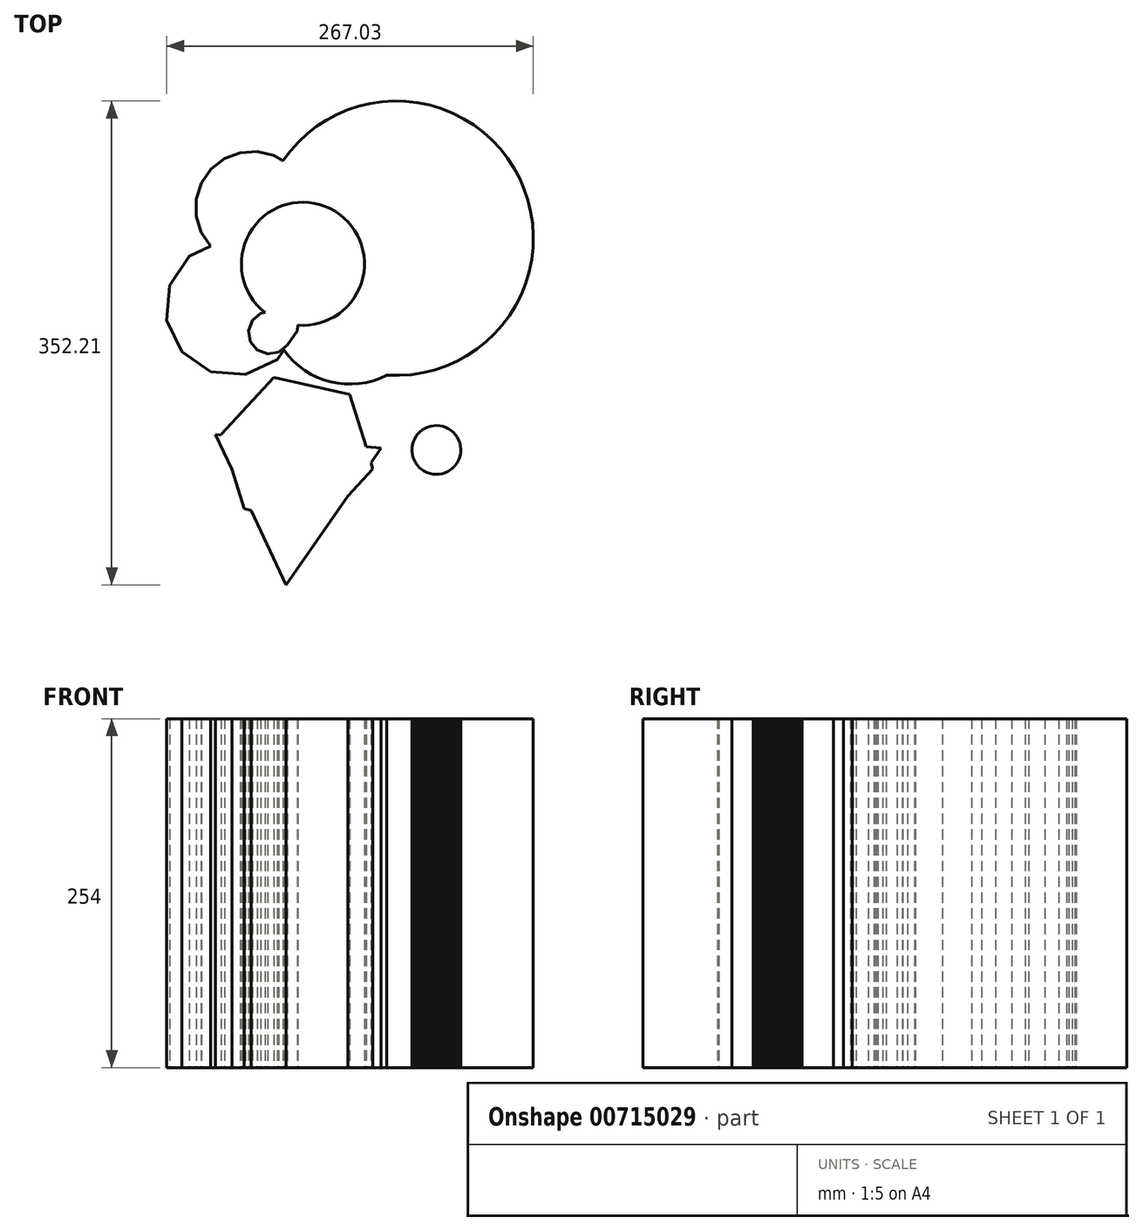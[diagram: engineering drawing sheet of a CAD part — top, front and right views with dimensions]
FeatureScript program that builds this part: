
annotation { "Feature Type Name" : "Feature", "Feature Type Description" : "" }
export const myFeature = defineFeature(function(context is Context, id is Id, definition is map)
    precondition{}
    {
        {
            var Q0;
            Q0=qCreatedBy(makeId("Top.planeOp"),FACE);
            var sketch = newSketch(context, id + "F0", { "sketchPlane" : qUnion([Q0])});
            skCircle(sketch, "E0", {"center": v(-130.21, -40.6) * mm, "radius": 44.83 * mm});
            skCircle(sketch, "E1", {"center": v(-96.12, -69.71) * mm, "radius": 58.54 * mm});
            skCircle(sketch, "E2", {"center": v(-62.25, -21.97) * mm, "radius": 99.89 * mm});
            skCircle(sketch, "E3.cCircle", {"center": v(-136.53, -204.62) * mm, "radius": 34.95 * mm, "construction": true});
            skLineSegment(sketch, "E3.0", {"start": v(-73.3, -174.81) * mm, "end": v(-142.33, -274.29) * mm});
            skLineSegment(sketch, "E3.1", {"start": v(-142.33, -274.29) * mm, "end": v(-193.96, -164.76) * mm});
            skLineSegment(sketch, "E3.2", {"start": v(-193.96, -164.76) * mm, "end": v(-73.3, -174.81) * mm});
            skPoint(sketch, "E3.0.midPoint", {"position": v(-107.81, -224.55) * mm});
            skCircle(sketch, "E4.cCircle", {"center": v(-154.3, -90.75) * mm, "radius": 15.01 * mm, "construction": true});
            skLineSegment(sketch, "E4.0", {"start": v(-141.63, -99.76) * mm, "end": v(-147.83, -104.88) * mm});
            skLineSegment(sketch, "E4.1", {"start": v(-147.83, -104.88) * mm, "end": v(-155.76, -106.22) * mm});
            skLineSegment(sketch, "E4.2", {"start": v(-155.76, -106.22) * mm, "end": v(-163.3, -103.41) * mm});
            skLineSegment(sketch, "E4.3", {"start": v(-163.3, -103.41) * mm, "end": v(-168.43, -97.21) * mm});
            skLineSegment(sketch, "E4.4", {"start": v(-168.43, -97.21) * mm, "end": v(-169.77, -89.28) * mm});
            skLineSegment(sketch, "E4.5", {"start": v(-169.77, -89.28) * mm, "end": v(-166.96, -81.74) * mm});
            skLineSegment(sketch, "E4.6", {"start": v(-166.96, -81.74) * mm, "end": v(-160.76, -76.61) * mm});
            skLineSegment(sketch, "E4.7", {"start": v(-160.76, -76.61) * mm, "end": v(-152.82, -75.27) * mm});
            skLineSegment(sketch, "E4.8", {"start": v(-152.82, -75.27) * mm, "end": v(-145.28, -78.08) * mm});
            skLineSegment(sketch, "E4.9", {"start": v(-145.28, -78.08) * mm, "end": v(-140.16, -84.28) * mm});
            skLineSegment(sketch, "E4.10", {"start": v(-140.16, -84.28) * mm, "end": v(-138.82, -92.22) * mm});
            skLineSegment(sketch, "E4.11", {"start": v(-138.82, -92.22) * mm, "end": v(-141.63, -99.76) * mm});
            skPoint(sketch, "E4.0.midPoint", {"position": v(-144.73, -102.32) * mm});
            skCircle(sketch, "E5.cCircle", {"center": v(-180.87, -72.71) * mm, "radius": 47.66 * mm, "construction": true});
            skLineSegment(sketch, "E5.0", {"start": v(-134.38, -89.24) * mm, "end": v(-148.87, -110.27) * mm});
            skLineSegment(sketch, "E5.1", {"start": v(-148.87, -110.27) * mm, "end": v(-171.94, -121.24) * mm});
            skLineSegment(sketch, "E5.2", {"start": v(-171.94, -121.24) * mm, "end": v(-197.4, -119.2) * mm});
            skLineSegment(sketch, "E5.3", {"start": v(-197.4, -119.2) * mm, "end": v(-218.43, -104.71) * mm});
            skLineSegment(sketch, "E5.4", {"start": v(-218.43, -104.71) * mm, "end": v(-229.4, -81.65) * mm});
            skLineSegment(sketch, "E5.5", {"start": v(-229.4, -81.65) * mm, "end": v(-227.36, -56.19) * mm});
            skLineSegment(sketch, "E5.6", {"start": v(-227.36, -56.19) * mm, "end": v(-212.87, -35.15) * mm});
            skLineSegment(sketch, "E5.7", {"start": v(-212.87, -35.15) * mm, "end": v(-189.8, -24.19) * mm});
            skLineSegment(sketch, "E5.8", {"start": v(-189.8, -24.19) * mm, "end": v(-164.34, -26.22) * mm});
            skLineSegment(sketch, "E5.9", {"start": v(-164.34, -26.22) * mm, "end": v(-143.31, -40.71) * mm});
            skLineSegment(sketch, "E5.10", {"start": v(-143.31, -40.71) * mm, "end": v(-132.34, -63.78) * mm});
            skLineSegment(sketch, "E5.11", {"start": v(-132.34, -63.78) * mm, "end": v(-134.38, -89.24) * mm});
            skPoint(sketch, "E5.0.midPoint", {"position": v(-141.63, -99.76) * mm});
            skCircle(sketch, "E6.cCircle", {"center": v(-166.96, 0) * mm, "radius": 40.85 * mm, "construction": true});
            skLineSegment(sketch, "E6.0", {"start": v(-164.21, -41.22) * mm, "end": v(-176.49, -40.2) * mm});
            skLineSegment(sketch, "E6.1", {"start": v(-176.49, -40.2) * mm, "end": v(-187.91, -35.6) * mm});
            skLineSegment(sketch, "E6.2", {"start": v(-187.91, -35.6) * mm, "end": v(-197.48, -27.85) * mm});
            skLineSegment(sketch, "E6.3", {"start": v(-197.48, -27.85) * mm, "end": v(-204.33, -17.62) * mm});
            skLineSegment(sketch, "E6.4", {"start": v(-204.33, -17.62) * mm, "end": v(-207.86, -5.82) * mm});
            skLineSegment(sketch, "E6.5", {"start": v(-207.86, -5.82) * mm, "end": v(-207.76, 6.5) * mm});
            skLineSegment(sketch, "E6.6", {"start": v(-207.76, 6.5) * mm, "end": v(-204.03, 18.24) * mm});
            skLineSegment(sketch, "E6.7", {"start": v(-204.03, 18.24) * mm, "end": v(-197, 28.35) * mm});
            skLineSegment(sketch, "E6.8", {"start": v(-197, 28.35) * mm, "end": v(-187.32, 35.95) * mm});
            skLineSegment(sketch, "E6.9", {"start": v(-187.32, 35.95) * mm, "end": v(-175.82, 40.36) * mm});
            skLineSegment(sketch, "E6.10", {"start": v(-175.82, 40.36) * mm, "end": v(-163.53, 41.17) * mm});
            skLineSegment(sketch, "E6.11", {"start": v(-163.53, 41.17) * mm, "end": v(-151.54, 38.33) * mm});
            skLineSegment(sketch, "E6.12", {"start": v(-151.54, 38.33) * mm, "end": v(-140.93, 32.09) * mm});
            skLineSegment(sketch, "E6.13", {"start": v(-140.93, 32.09) * mm, "end": v(-132.63, 22.99) * mm});
            skLineSegment(sketch, "E6.14", {"start": v(-132.63, 22.99) * mm, "end": v(-127.38, 11.85) * mm});
            skLineSegment(sketch, "E6.15", {"start": v(-127.38, 11.85) * mm, "end": v(-125.64, -0.34) * mm});
            skLineSegment(sketch, "E6.16", {"start": v(-125.64, -0.34) * mm, "end": v(-127.58, -12.5) * mm});
            skLineSegment(sketch, "E6.17", {"start": v(-127.58, -12.5) * mm, "end": v(-133.02, -23.56) * mm});
            skLineSegment(sketch, "E6.18", {"start": v(-133.02, -23.56) * mm, "end": v(-141.47, -32.52) * mm});
            skLineSegment(sketch, "E6.19", {"start": v(-141.47, -32.52) * mm, "end": v(-152.19, -38.58) * mm});
            skLineSegment(sketch, "E6.20", {"start": v(-152.19, -38.58) * mm, "end": v(-164.21, -41.22) * mm});
            skPoint(sketch, "E6.0.midPoint", {"position": v(-170.35, -40.71) * mm});
            skCircle(sketch, "E7.cCircle", {"center": v(-33.01, -176.15) * mm, "radius": 17.77 * mm, "construction": true});
            skLineSegment(sketch, "E7.0", {"start": v(-32.65, -158.35) * mm, "end": v(-30.42, -158.53) * mm});
            skLineSegment(sketch, "E7.1", {"start": v(-30.42, -158.53) * mm, "end": v(-28.24, -159) * mm});
            skLineSegment(sketch, "E7.2", {"start": v(-28.24, -159) * mm, "end": v(-26.12, -159.73) * mm});
            skLineSegment(sketch, "E7.3", {"start": v(-26.12, -159.73) * mm, "end": v(-24.12, -160.72) * mm});
            skLineSegment(sketch, "E7.4", {"start": v(-24.12, -160.72) * mm, "end": v(-22.26, -161.96) * mm});
            skLineSegment(sketch, "E7.5", {"start": v(-22.26, -161.96) * mm, "end": v(-20.56, -163.42) * mm});
            skLineSegment(sketch, "E7.6", {"start": v(-20.56, -163.42) * mm, "end": v(-19.07, -165.08) * mm});
            skLineSegment(sketch, "E7.7", {"start": v(-19.07, -165.08) * mm, "end": v(-17.8, -166.91) * mm});
            skLineSegment(sketch, "E7.8", {"start": v(-17.8, -166.91) * mm, "end": v(-16.75, -168.9) * mm});
            skLineSegment(sketch, "E7.9", {"start": v(-16.75, -168.9) * mm, "end": v(-15.97, -171) * mm});
            skLineSegment(sketch, "E7.10", {"start": v(-15.97, -171) * mm, "end": v(-15.46, -173.17) * mm});
            skLineSegment(sketch, "E7.11", {"start": v(-15.46, -173.17) * mm, "end": v(-15.23, -175.39) * mm});
            skLineSegment(sketch, "E7.12", {"start": v(-15.23, -175.39) * mm, "end": v(-15.27, -177.62) * mm});
            skLineSegment(sketch, "E7.13", {"start": v(-15.27, -177.62) * mm, "end": v(-15.6, -179.84) * mm});
            skLineSegment(sketch, "E7.14", {"start": v(-15.6, -179.84) * mm, "end": v(-16.2, -182) * mm});
            skLineSegment(sketch, "E7.15", {"start": v(-16.2, -182) * mm, "end": v(-17.06, -184.05) * mm});
            skLineSegment(sketch, "E7.16", {"start": v(-17.06, -184.05) * mm, "end": v(-18.18, -185.99) * mm});
            skLineSegment(sketch, "E7.17", {"start": v(-18.18, -185.99) * mm, "end": v(-19.53, -187.77) * mm});
            skLineSegment(sketch, "E7.18", {"start": v(-19.53, -187.77) * mm, "end": v(-21.1, -189.37) * mm});
            skLineSegment(sketch, "E7.19", {"start": v(-21.1, -189.37) * mm, "end": v(-22.84, -190.76) * mm});
            skLineSegment(sketch, "E7.20", {"start": v(-22.84, -190.76) * mm, "end": v(-24.75, -191.92) * mm});
            skLineSegment(sketch, "E7.21", {"start": v(-24.75, -191.92) * mm, "end": v(-26.8, -192.83) * mm});
            skLineSegment(sketch, "E7.22", {"start": v(-26.8, -192.83) * mm, "end": v(-28.93, -193.48) * mm});
            skLineSegment(sketch, "E7.23", {"start": v(-28.93, -193.48) * mm, "end": v(-31.14, -193.85) * mm});
            skLineSegment(sketch, "E7.24", {"start": v(-31.14, -193.85) * mm, "end": v(-33.37, -193.95) * mm});
            skLineSegment(sketch, "E7.25", {"start": v(-33.37, -193.95) * mm, "end": v(-35.6, -193.76) * mm});
            skLineSegment(sketch, "E7.26", {"start": v(-35.6, -193.76) * mm, "end": v(-37.79, -193.3) * mm});
            skLineSegment(sketch, "E7.27", {"start": v(-37.79, -193.3) * mm, "end": v(-39.9, -192.56) * mm});
            skLineSegment(sketch, "E7.28", {"start": v(-39.9, -192.56) * mm, "end": v(-41.9, -191.57) * mm});
            skLineSegment(sketch, "E7.29", {"start": v(-41.9, -191.57) * mm, "end": v(-43.76, -190.34) * mm});
            skLineSegment(sketch, "E7.30", {"start": v(-43.76, -190.34) * mm, "end": v(-45.46, -188.88) * mm});
            skLineSegment(sketch, "E7.31", {"start": v(-45.46, -188.88) * mm, "end": v(-46.95, -187.22) * mm});
            skLineSegment(sketch, "E7.32", {"start": v(-46.95, -187.22) * mm, "end": v(-48.23, -185.38) * mm});
            skLineSegment(sketch, "E7.33", {"start": v(-48.23, -185.38) * mm, "end": v(-49.27, -183.4) * mm});
            skLineSegment(sketch, "E7.34", {"start": v(-49.27, -183.4) * mm, "end": v(-50.05, -181.3) * mm});
            skLineSegment(sketch, "E7.35", {"start": v(-50.05, -181.3) * mm, "end": v(-50.56, -179.13) * mm});
            skLineSegment(sketch, "E7.36", {"start": v(-50.56, -179.13) * mm, "end": v(-50.8, -176.9) * mm});
            skLineSegment(sketch, "E7.37", {"start": v(-50.8, -176.9) * mm, "end": v(-50.75, -174.67) * mm});
            skLineSegment(sketch, "E7.38", {"start": v(-50.75, -174.67) * mm, "end": v(-50.43, -172.46) * mm});
            skLineSegment(sketch, "E7.39", {"start": v(-50.43, -172.46) * mm, "end": v(-49.83, -170.3) * mm});
            skLineSegment(sketch, "E7.40", {"start": v(-49.83, -170.3) * mm, "end": v(-48.96, -168.24) * mm});
            skLineSegment(sketch, "E7.41", {"start": v(-48.96, -168.24) * mm, "end": v(-47.85, -166.3) * mm});
            skLineSegment(sketch, "E7.42", {"start": v(-47.85, -166.3) * mm, "end": v(-46.5, -164.52) * mm});
            skLineSegment(sketch, "E7.43", {"start": v(-46.5, -164.52) * mm, "end": v(-44.93, -162.93) * mm});
            skLineSegment(sketch, "E7.44", {"start": v(-44.93, -162.93) * mm, "end": v(-43.18, -161.54) * mm});
            skLineSegment(sketch, "E7.45", {"start": v(-43.18, -161.54) * mm, "end": v(-41.27, -160.38) * mm});
            skLineSegment(sketch, "E7.46", {"start": v(-41.27, -160.38) * mm, "end": v(-39.23, -159.47) * mm});
            skLineSegment(sketch, "E7.47", {"start": v(-39.23, -159.47) * mm, "end": v(-37.09, -158.82) * mm});
            skLineSegment(sketch, "E7.48", {"start": v(-37.09, -158.82) * mm, "end": v(-34.88, -158.44) * mm});
            skLineSegment(sketch, "E7.49", {"start": v(-34.88, -158.44) * mm, "end": v(-32.65, -158.35) * mm});
            skPoint(sketch, "E7.0.midPoint", {"position": v(-31.54, -158.44) * mm});
            skCircle(sketch, "E8.cCircle", {"center": v(-134.52, -177.38) * mm, "radius": 49.09 * mm, "construction": true});
            skLineSegment(sketch, "E8.0", {"start": v(-96.04, -135.76) * mm, "end": v(-79.24, -189.9) * mm});
            skLineSegment(sketch, "E8.1", {"start": v(-79.24, -189.9) * mm, "end": v(-117.72, -231.52) * mm});
            skLineSegment(sketch, "E8.2", {"start": v(-117.72, -231.52) * mm, "end": v(-173, -219) * mm});
            skLineSegment(sketch, "E8.3", {"start": v(-173, -219) * mm, "end": v(-189.8, -164.87) * mm});
            skLineSegment(sketch, "E8.4", {"start": v(-189.8, -164.87) * mm, "end": v(-151.32, -123.25) * mm});
            skLineSegment(sketch, "E8.5", {"start": v(-151.32, -123.25) * mm, "end": v(-96.04, -135.76) * mm});
            skPoint(sketch, "E8.0.midPoint", {"position": v(-87.64, -162.83) * mm});
            skSolve(sketch);
        }
        {
            var Q0;
            Q0 = qSketchRegion(id + "F0", true);
            extrude(context, id + "F1", {"entities" : qUnion([Q0]), "depth" : 254 * mm, "offsetDistance" : 25.4 * mm});
        }
    });
